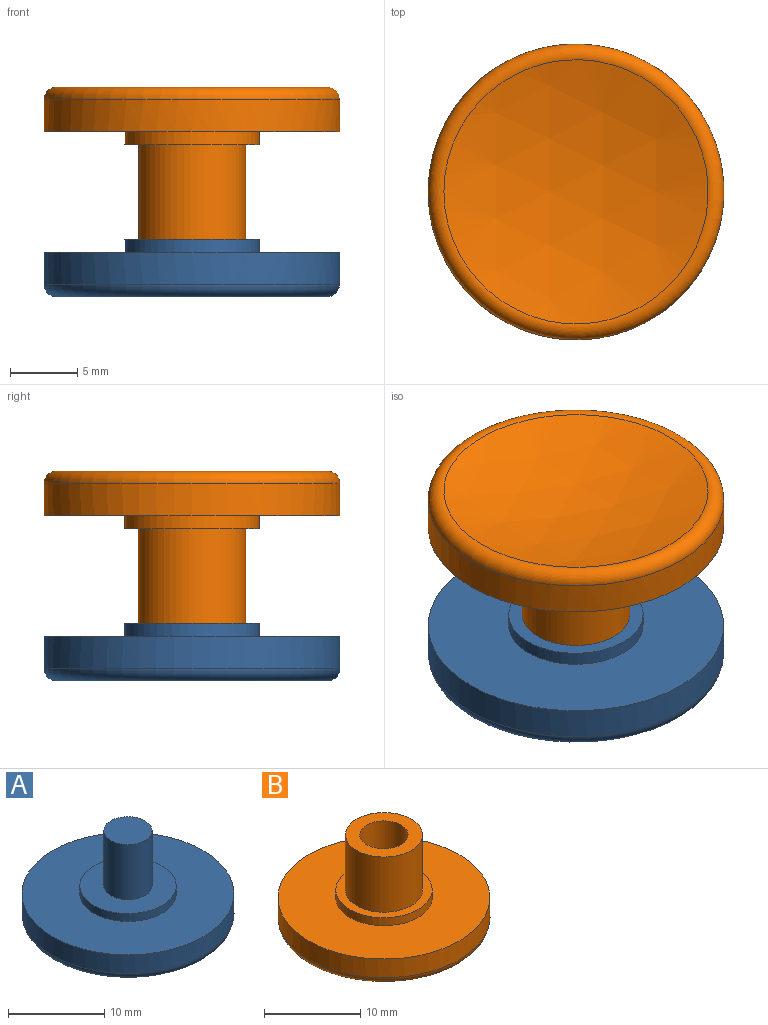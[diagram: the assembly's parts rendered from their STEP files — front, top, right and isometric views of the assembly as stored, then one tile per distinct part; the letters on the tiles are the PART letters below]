
ASSEMBLY  parts=2 mates=1
PART A: 8 faces, bbox 23.8x23.8x12.7 mm
  f0: cylinder r=11mm len=22mm, axis (0,0,-1), area 164.6mm2, adj f1,f5
  f1: plane 22x22mm, normal (0,0,1), area 301.6mm2, adj f0,f2
  f2: cylinder r=5mm len=10mm, axis (0,0,-1), area 31.4mm2, adj f1,f3
  f3: plane 10x10mm, normal (0,0,1), area 58.9mm2, adj f2,f6
  f4: sphere r=34mm, area 310.1mm2, adj f5
  f5: torus R=10.09mm, axis (0,0,-1), area 112.4mm2, adj f0,f4
  f6: cylinder r=2.5mm len=7mm, axis (0,0,1), area 110mm2, adj f3,f7
  f7: plane 5x5mm, normal (0,0,1), area 19.6mm2, adj f6
PART B: 10 faces, bbox 23.8x23.8x12.7 mm
  f0: cylinder r=11mm len=22mm, axis (0,0,-1), area 164.6mm2, adj f1,f7
  f1: plane 22x22mm, normal (0,0,1), area 301.6mm2, adj f0,f2
  f2: cylinder r=5mm len=10mm, axis (0,0,-1), area 31.4mm2, adj f1,f3
  f3: plane 10x10mm, normal (0,0,1), area 28.3mm2, adj f2,f4
  f4: cylinder r=4mm len=8mm, axis (0,0,-1), area 175.9mm2, adj f3,f5
  f5: plane 8x8mm, normal (0,0,1), area 30.6mm2, adj f4,f8
  f6: sphere r=34mm, area 310.1mm2, adj f7
  f7: torus R=10.09mm, axis (0,0,-1), area 112.4mm2, adj f0,f6
  f8: cylinder r=2.5mm len=7mm, axis (0,0,1), area 110mm2, adj f5,f9
  f9: plane 5x5mm, normal (0,0,1), area 19.6mm2, adj f8
PLACE A t=(4.49,-5.2,7.93)mm
PLACE B rot(axis=(1,0,0),180deg) t=(-26.21,122.92,23.93)mm
MATE pin_slot B.f0 <-> A.f0  axis (0,0,-1) through (33.21,58.86,12.43)mm
